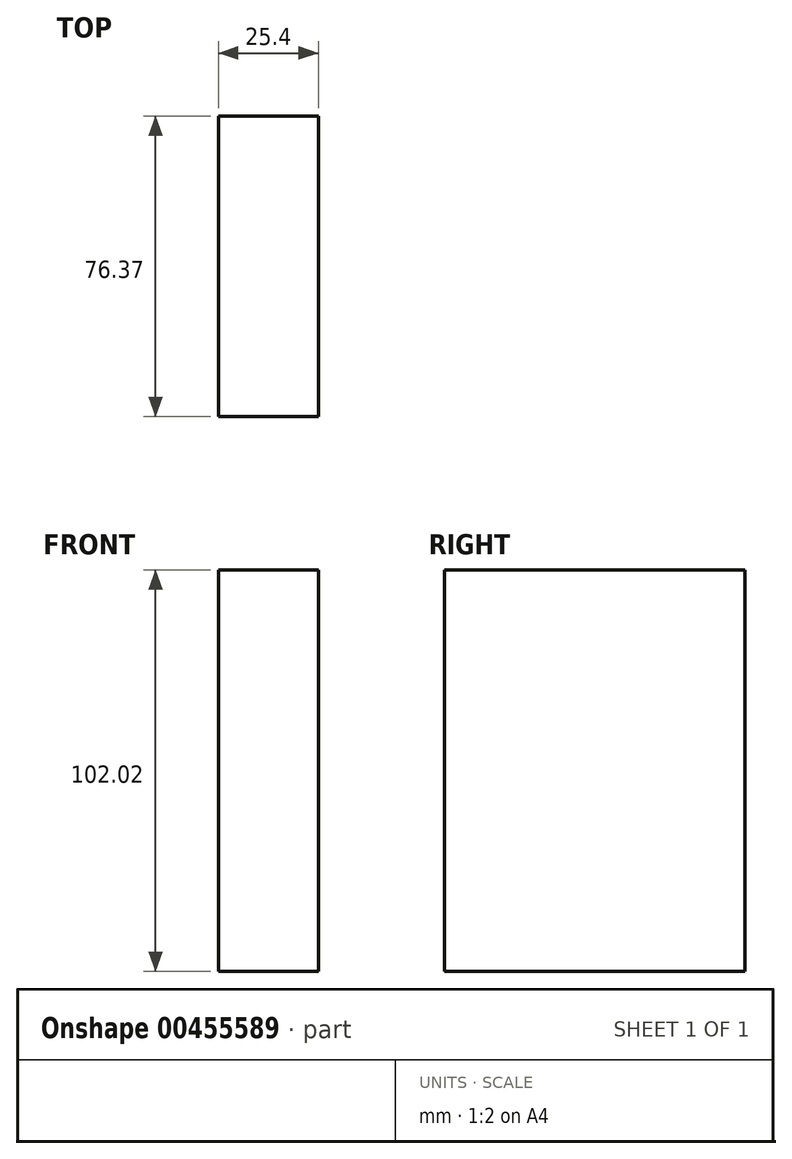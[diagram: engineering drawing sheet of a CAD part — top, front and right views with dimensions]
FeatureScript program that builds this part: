
annotation { "Feature Type Name" : "Feature", "Feature Type Description" : "" }
export const myFeature = defineFeature(function(context is Context, id is Id, definition is map)
    precondition{}
    {
        {
            var Q0;
            Q0=qCreatedBy(makeId("Right.planeOp"),FACE);
            var sketch = newSketch(context, id + "F0", { "sketchPlane" : qUnion([Q0])});
            skLineSegment(sketch, "E0.bottom", {"start": v(15.74, -26.09) * mm, "end": v(-60.63, -26.09) * mm});
            skLineSegment(sketch, "E0.top", {"start": v(15.74, 75.93) * mm, "end": v(-60.63, 75.93) * mm});
            skLineSegment(sketch, "E0.left", {"start": v(15.74, -26.09) * mm, "end": v(15.74, 75.93) * mm});
            skLineSegment(sketch, "E0.right", {"start": v(-60.63, -26.09) * mm, "end": v(-60.63, 75.93) * mm});
            skSolve(sketch);
        }
        {
            var Q0;
            Q0 = qSketchRegion(id + "F0", true);
            extrude(context, id + "F1", {"entities" : qUnion([Q0]), "depth" : 25.4 * mm});
        }
    });
